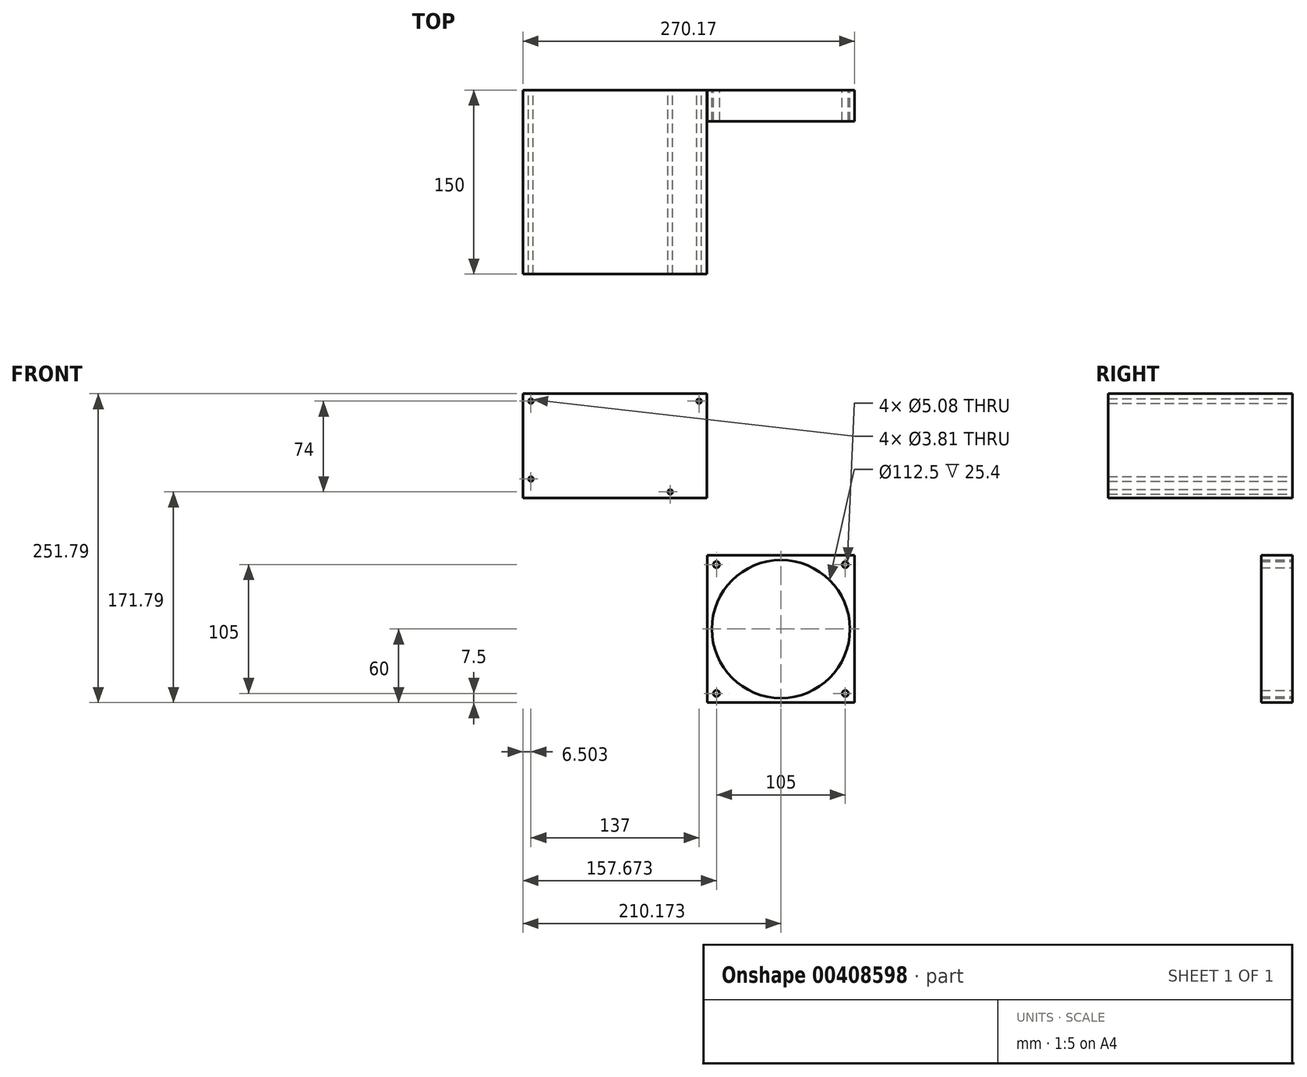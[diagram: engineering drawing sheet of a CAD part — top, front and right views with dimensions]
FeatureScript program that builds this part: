
annotation { "Feature Type Name" : "Feature", "Feature Type Description" : "" }
export const myFeature = defineFeature(function(context is Context, id is Id, definition is map)
    precondition{}
    {
        {
            var Q0;
            Q0=qCreatedBy(makeId("Front.planeOp"),FACE);
            var sketch = newSketch(context, id + "F0", { "sketchPlane" : qUnion([Q0])});
            skLineSegment(sketch, "E0.bottom", {"start": v(-63.39, 127.4) * mm, "end": v(86.61, 127.4) * mm});
            skLineSegment(sketch, "E0.top", {"start": v(-63.39, 42.4) * mm, "end": v(86.61, 42.4) * mm});
            skLineSegment(sketch, "E0.left", {"start": v(-63.39, 127.4) * mm, "end": v(-63.39, 42.4) * mm});
            skLineSegment(sketch, "E0.right", {"start": v(86.61, 127.4) * mm, "end": v(86.61, 42.4) * mm});
            skCircle(sketch, "E1", {"center": v(-56.89, 121.4) * mm, "radius": 1.9 * mm});
            skCircle(sketch, "E2", {"center": v(80.11, 121.4) * mm, "radius": 1.9 * mm});
            skCircle(sketch, "E3", {"center": v(56.61, 47.4) * mm, "radius": 1.9 * mm});
            skCircle(sketch, "E4", {"center": v(-56.89, 57.9) * mm, "radius": 1.9 * mm});
            skSolve(sketch);
        }
        {
            var Q0;
            Q0=makeQuery(id+"F0.imprint","IMPRINT",FACE,{"disambiguationData":[TD([[makeQuery(id+"F0.imprint","IMPRINT",EDGE,{"derivedFrom":sQuery(id+"F0.wireOp",EDGE,"E0.bottom")}),-1.0]])]});
            extrude(context, id + "F1", {"entities" : qUnion([Q0]), "depth" : 150 * mm, "offsetDistance" : 25.4 * mm});
        }
        {
            var Q0;
            Q0=qCreatedBy(makeId("Front.planeOp"),FACE);
            var sketch = newSketch(context, id + "F2", { "sketchPlane" : qUnion([Q0])});
            skLineSegment(sketch, "E5.bottom", {"start": v(86.78, -4.4) * mm, "end": v(206.78, -4.4) * mm});
            skLineSegment(sketch, "E5.top", {"start": v(86.78, -124.4) * mm, "end": v(206.78, -124.4) * mm});
            skLineSegment(sketch, "E5.left", {"start": v(86.78, -4.4) * mm, "end": v(86.78, -124.4) * mm});
            skLineSegment(sketch, "E5.right", {"start": v(206.78, -4.4) * mm, "end": v(206.78, -124.4) * mm});
            skCircle(sketch, "E6", {"center": v(94.28, -11.9) * mm, "radius": 2.54 * mm});
            skCircle(sketch, "E7.0.1.0", {"center": v(94.28, -116.9) * mm, "radius": 2.54 * mm});
            skCircle(sketch, "E7.1.0.0", {"center": v(199.28, -11.9) * mm, "radius": 2.54 * mm});
            skCircle(sketch, "E7.1.1.0", {"center": v(199.28, -116.9) * mm, "radius": 2.54 * mm});
            skLineSegment(sketch, "E7.direction1", {"start": v(94.28, -11.9) * mm, "end": v(199.28, -11.9) * mm, "construction": true});
            skLineSegment(sketch, "E7.direction2", {"start": v(94.28, -11.9) * mm, "end": v(94.28, -116.9) * mm, "construction": true});
            skPoint(sketch, "E8", {"position": v(146.78, -4.4) * mm});
            skPoint(sketch, "E9", {"position": v(146.78, -11.9) * mm});
            skPoint(sketch, "E10", {"position": v(86.78, -64.4) * mm});
            skPoint(sketch, "E11", {"position": v(94.28, -64.4) * mm});
            skCircle(sketch, "E12", {"center": v(146.78, -64.4) * mm, "radius": 56.25 * mm});
            skLineSegment(sketch, "E13", {"start": v(146.78, -4.4) * mm, "end": v(146.78, -11.9) * mm, "construction": true});
            skPoint(sketch, "E14", {"position": v(146.78, -8.15) * mm});
            skSolve(sketch);
        }
        {
            var Q0;
            Q0 = qSketchRegion(id + "F2", true);
            extrude(context, id + "F3", {"entities" : qUnion([Q0]), "depth" : 25.4 * mm, "offsetDistance" : 25.4 * mm});
        }
    });
